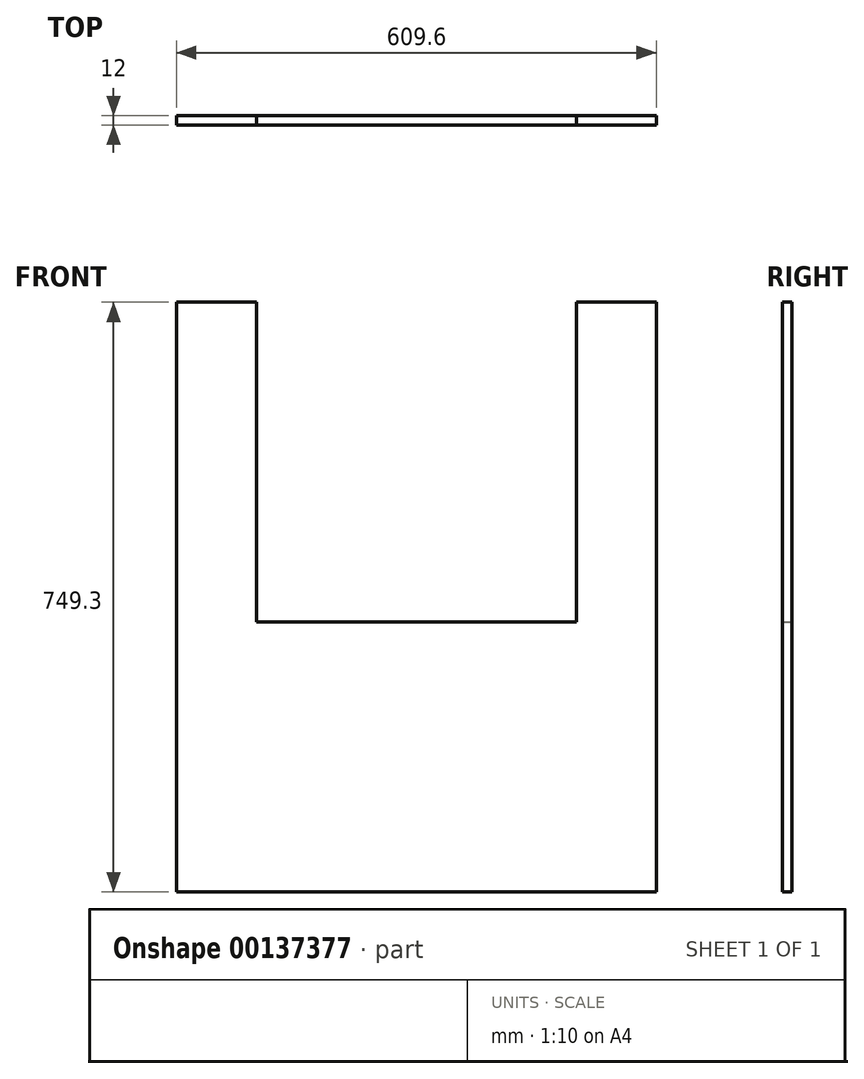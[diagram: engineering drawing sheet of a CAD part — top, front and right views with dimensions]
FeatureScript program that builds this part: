
annotation { "Feature Type Name" : "Feature", "Feature Type Description" : "" }
export const myFeature = defineFeature(function(context is Context, id is Id, definition is map)
    precondition{}
    {
        {
            var Q0;
            Q0=qCreatedBy(makeId("Front.planeOp"),FACE);
            var sketch = newSketch(context, id + "F0", { "sketchPlane" : qUnion([Q0])});
            skLineSegment(sketch, "E0.bottom", {"start": v(-305.57, 365.2) * mm, "end": v(304.03, 365.2) * mm});
            skLineSegment(sketch, "E0.top", {"start": v(-305.57, -384.1) * mm, "end": v(304.03, -384.1) * mm});
            skLineSegment(sketch, "E0.left", {"start": v(-305.57, 365.2) * mm, "end": v(-305.57, -384.1) * mm});
            skLineSegment(sketch, "E0.right", {"start": v(304.03, 365.2) * mm, "end": v(304.03, -384.1) * mm});
            skLineSegment(sketch, "E1.bottom", {"start": v(-203.97, 365.2) * mm, "end": v(202.43, 365.2) * mm});
            skLineSegment(sketch, "E1.top", {"start": v(-203.97, -41.2) * mm, "end": v(202.43, -41.2) * mm});
            skLineSegment(sketch, "E1.left", {"start": v(-203.97, 365.2) * mm, "end": v(-203.97, -41.2) * mm});
            skLineSegment(sketch, "E1.right", {"start": v(202.43, 365.2) * mm, "end": v(202.43, -41.2) * mm});
            skSolve(sketch);
        }
        {
            var Q0;
            Q0=makeQuery(id+"F0.imprint","IMPRINT",FACE,{"disambiguationData":[TD([[makeQuery(id+"F0.imprint","IMPRINT",EDGE,{"derivedFrom":sQuery(id+"F0.wireOp",EDGE,"E0.top")}),1.0]])]});
            extrude(context, id + "F1", {"entities" : qUnion([Q0]), "depth" : 12 * mm});
        }
    });
